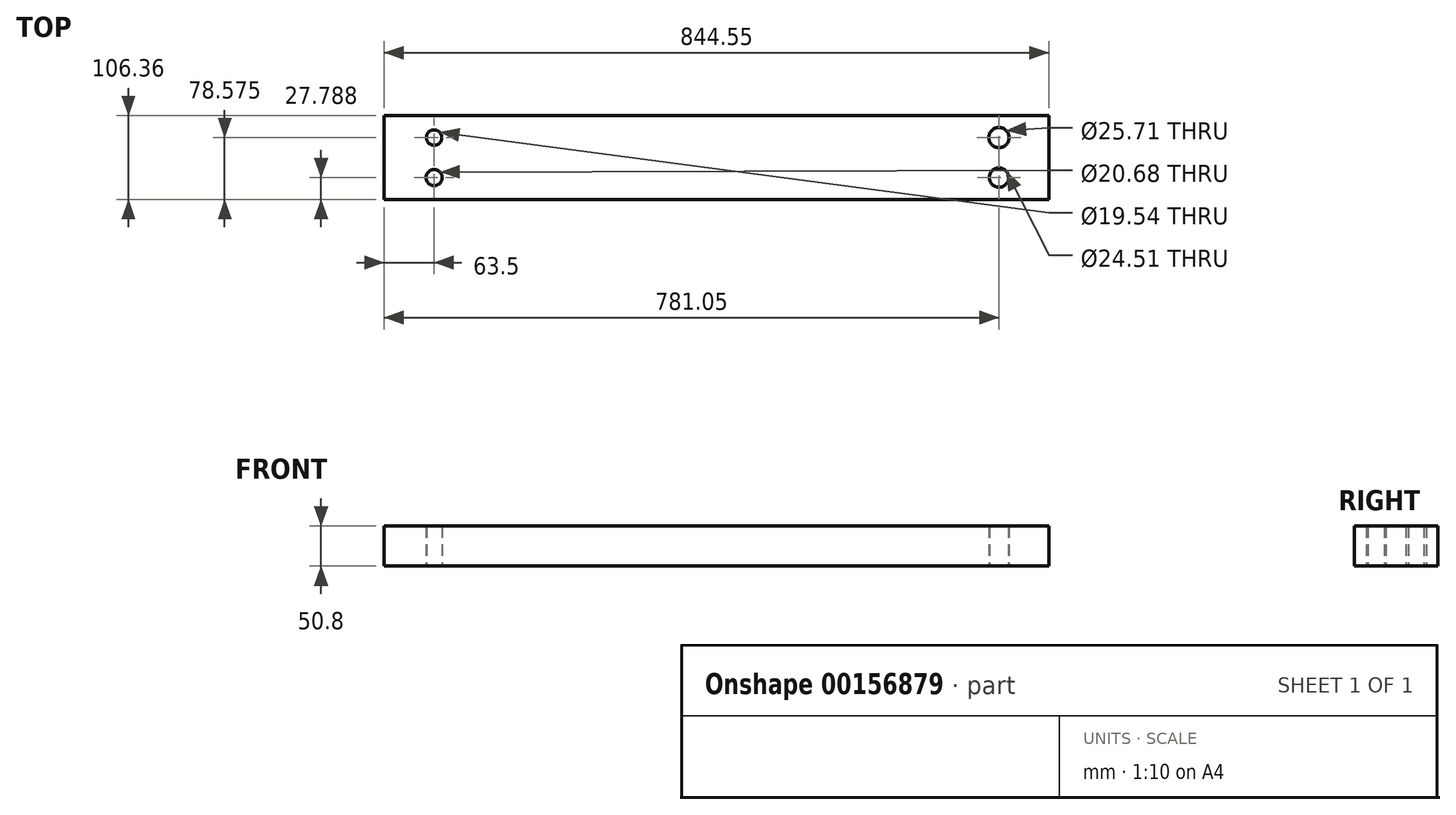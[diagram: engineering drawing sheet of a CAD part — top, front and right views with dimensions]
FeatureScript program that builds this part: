
annotation { "Feature Type Name" : "Feature", "Feature Type Description" : "" }
export const myFeature = defineFeature(function(context is Context, id is Id, definition is map)
    precondition{}
    {
        {
            var Q0;
            Q0=qCreatedBy(makeId("Top.planeOp"),FACE);
            var sketch = newSketch(context, id + "F0", { "sketchPlane" : qUnion([Q0])});
            skLineSegment(sketch, "E0.bottom", {"start": v(0, 0) * mm, "end": v(844.55, 0) * mm});
            skLineSegment(sketch, "E0.top", {"start": v(0, 106.36) * mm, "end": v(844.55, 106.36) * mm});
            skLineSegment(sketch, "E0.left", {"start": v(0, 0) * mm, "end": v(0, 106.36) * mm});
            skLineSegment(sketch, "E0.right", {"start": v(844.55, 0) * mm, "end": v(844.55, 106.36) * mm});
            skLineSegment(sketch, "E1.0", {"start": v(781.05, 0) * mm, "end": v(781.05, 106.36) * mm, "construction": true});
            skLineSegment(sketch, "E2.0", {"start": v(0, 78.57) * mm, "end": v(844.55, 78.57) * mm, "construction": true});
            skLineSegment(sketch, "E3.0", {"start": v(0, 27.79) * mm, "end": v(844.55, 27.79) * mm, "construction": true});
            skLineSegment(sketch, "E4.0", {"start": v(63.5, 0) * mm, "end": v(63.5, 106.36) * mm, "construction": true});
            skCircle(sketch, "E5", {"center": v(63.5, 78.57) * mm, "radius": 9.77 * mm});
            skCircle(sketch, "E6", {"center": v(63.5, 27.79) * mm, "radius": 10.34 * mm});
            skCircle(sketch, "E7", {"center": v(781.05, 78.57) * mm, "radius": 12.85 * mm});
            skCircle(sketch, "E8", {"center": v(781.05, 27.79) * mm, "radius": 12.26 * mm});
            skSolve(sketch);
        }
        {
            var Q0;
            Q0=makeQuery(id+"F0.imprint","IMPRINT",FACE,{"disambiguationData":[TD([[makeQuery(id+"F0.imprint","IMPRINT",EDGE,{"derivedFrom":sQuery(id+"F0.wireOp",EDGE,"E0.bottom")}),1.0]])]});
            extrude(context, id + "F1", {"entities" : qUnion([Q0]), "depth" : 50.8 * mm});
        }
    });
